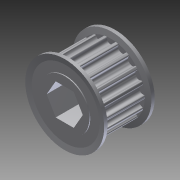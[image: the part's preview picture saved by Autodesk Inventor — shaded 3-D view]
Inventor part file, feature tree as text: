
AUTODESK INVENTOR PART (.ipt)
format: ipt  version: 2014 (Build 180170000, 170)  size: 654,336 bytes
history: native  units: in
note: dims shown in document units (in); Inventor stores cm internally (conversion verified against a paired STEP export)
features: mirror x1, other x1, imported_body x1
ambient origin geometry x8: Origin, YZ Plane, XZ Plane, XY Plane, X Axis, Y Axis, Z Axis, Center Point
bodies: Body1 (feature_tree)
feature tree (3):
  mirror  "Mirror1"
  other  "217-3226-STEP1"
  imported_body  "Base1"
